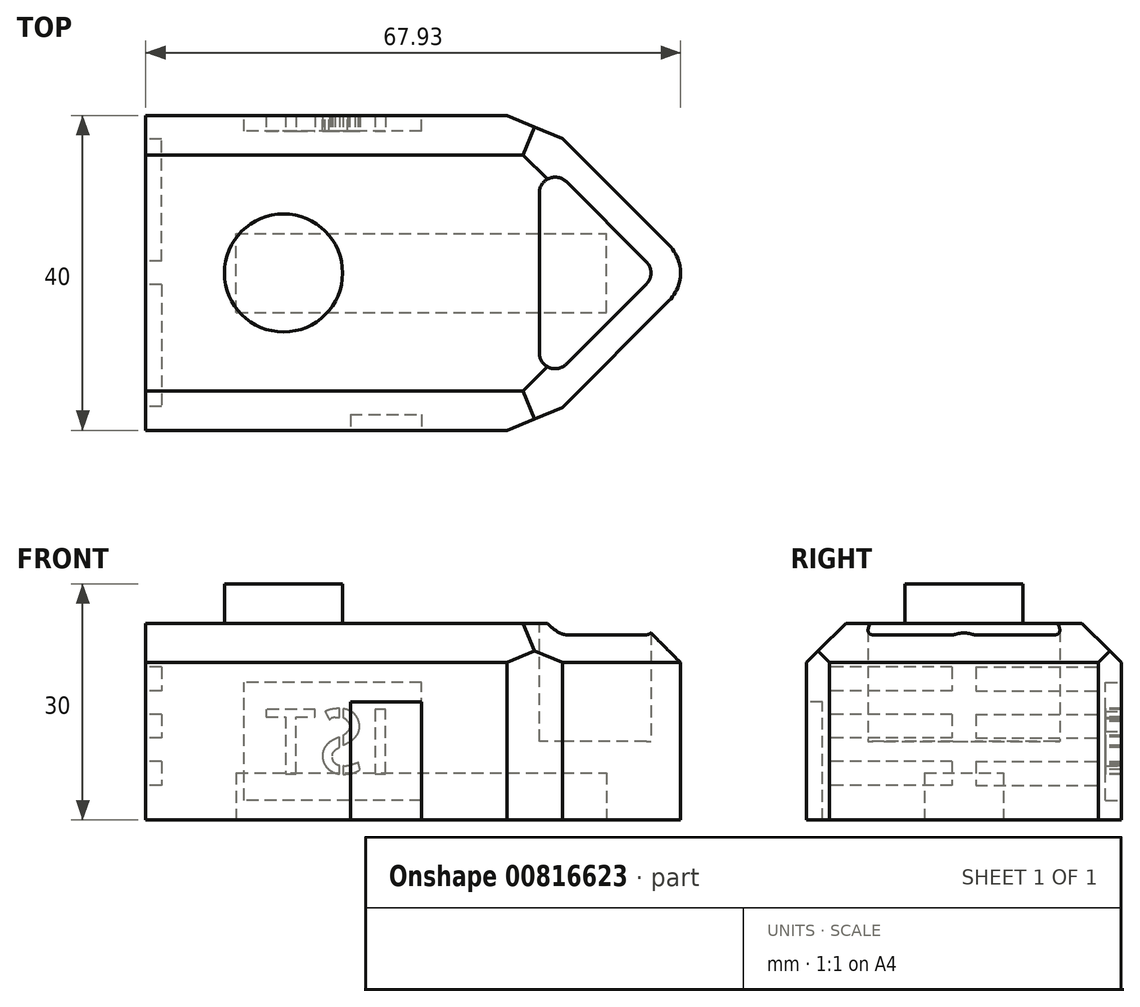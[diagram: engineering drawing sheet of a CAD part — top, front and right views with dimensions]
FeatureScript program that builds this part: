
annotation { "Feature Type Name" : "Feature", "Feature Type Description" : "" }
export const myFeature = defineFeature(function(context is Context, id is Id, definition is map)
    precondition{}
    {
        {
            var Q0;
            Q0=qCreatedBy(makeId("Top.planeOp"),FACE);
            var sketch = newSketch(context, id + "F0", { "sketchPlane" : qUnion([Q0])});
            skLineSegment(sketch, "E0.bottom", {"start": v(-35, 20) * mm, "end": v(35, 20) * mm});
            skLineSegment(sketch, "E0.top", {"start": v(-35, -20) * mm, "end": v(35, -20) * mm});
            skLineSegment(sketch, "E0.left", {"start": v(-35, 20) * mm, "end": v(-35, -20) * mm});
            skLineSegment(sketch, "E0.right", {"start": v(35, 20) * mm, "end": v(35, -20) * mm});
            skPoint(sketch, "E0.middle", {"position": v(0, 0) * mm});
            skSolve(sketch);
        }
        {
            var Q0;
            Q0 = qSketchRegion(id + "F0", true);
            extrude(context, id + "F1", {"entities" : qUnion([Q0]), "depth" : 25 * mm, "offsetDistance" : 25 * mm});
        }
        {
            var Q0;
            Q0=makeQuery(id+"F1.opExtrude","SWEPT_EDGE",EDGE,{"disambiguationData":[OSD([sQuery(id+"F0.wireOp",EDGE,"E0.top"),sQuery(id+"F0.wireOp",EDGE,"E0.right")])]});
            var Q1;
            Q1=makeQuery(id+"F1.opExtrude","SWEPT_EDGE",EDGE,{"disambiguationData":[OSD([sQuery(id+"F0.wireOp",EDGE,"E0.bottom"),sQuery(id+"F0.wireOp",EDGE,"E0.right")])]});
            chamfer(context, id + "F2", {"entities" : qUnion([Q0, Q1]), "width" : 20 * mm, "tangentPropagation" : true});
        }
        {
            var Q0;
            {var subQ0=sQuery(id+"F0.wireOp",EDGE,"E0.right");Q0=makeQuery(id+"F2.opChamfer","BLEND_EDGE",EDGE,{"blendedFrom":[makeQuery(id+"F1.opExtrude","SWEPT_EDGE",EDGE,{"disambiguationData":[OSD([sQuery(id+"F0.wireOp",EDGE,"E0.bottom"),subQ0])]}),makeQuery(id+"F1.opExtrude","SWEPT_EDGE",EDGE,{"disambiguationData":[OSD([sQuery(id+"F0.wireOp",EDGE,"E0.top"),subQ0])]})],"blendedInto":[]});}
            fillet(context, id + "F3", {"entities" : qUnion([Q0]), "radius" : 5 * mm, "tangentPropagation" : true, "allowEdgeOverflow" : false});
        }
        {
            var Q0;
            Q0=makeQuery(id+"F1.opExtrude","CAP_FACE",FACE,{"disambiguationData":[OSD([sQuery(id+"F0.wireOp",EDGE,"E0.bottom"),sQuery(id+"F0.wireOp",EDGE,"E0.top"),sQuery(id+"F0.wireOp",EDGE,"E0.left"),sQuery(id+"F0.wireOp",EDGE,"E0.right")])],"isStart":true});
            var sketch = newSketch(context, id + "F4", { "sketchPlane" : qUnion([Q0])});
            skLineSegment(sketch, "E1.bottom", {"start": v(-23.5, 5) * mm, "end": v(23.5, 5) * mm});
            skLineSegment(sketch, "E1.top", {"start": v(-23.5, -5) * mm, "end": v(23.5, -5) * mm});
            skLineSegment(sketch, "E1.left", {"start": v(-23.5, 5) * mm, "end": v(-23.5, -5) * mm});
            skLineSegment(sketch, "E1.right", {"start": v(23.5, 5) * mm, "end": v(23.5, -5) * mm});
            skPoint(sketch, "E1.middle", {"position": v(0, 0) * mm});
            skSolve(sketch);
        }
        {
            var Q0;
            Q0=makeQuery(id+"F4.imprint","IMPRINT",FACE,{"disambiguationData":[TD([[makeQuery(id+"F4.imprint","IMPRINT",EDGE,{"derivedFrom":sQuery(id+"F4.wireOp",EDGE,"E1.bottom")}),-1.0]])]});
            extrude(context, id + "F5", {"entities" : qUnion([Q0]), "operationType" : NewBodyOperationType.REMOVE, "oppositeDirection" : true, "depth" : 6 * mm, "offsetDistance" : 25 * mm});
        }
        {
            var Q0;
            Q0=makeQuery(id+"F1.opExtrude","CAP_FACE",FACE,{"disambiguationData":[OSD([sQuery(id+"F0.wireOp",EDGE,"E0.bottom"),sQuery(id+"F0.wireOp",EDGE,"E0.top"),sQuery(id+"F0.wireOp",EDGE,"E0.left"),sQuery(id+"F0.wireOp",EDGE,"E0.right")])],"isStart":false});
            var sketch = newSketch(context, id + "F6", { "sketchPlane" : qUnion([Q0])});
            skPoint(sketch, "E2", {"position": v(15, 0) * mm});
            skLineSegment(sketch, "E3", {"start": v(15, 0) * mm, "end": v(15, 15) * mm});
            skLineSegment(sketch, "E4", {"start": v(15, 15) * mm, "end": v(15, -15) * mm});
            skLineSegment(sketch, "E5", {"start": v(15, 15) * mm, "end": v(30, 0) * mm});
            skLineSegment(sketch, "E6", {"start": v(30, 0) * mm, "end": v(15, -15) * mm});
            skPoint(sketch, "E7.orphan", {"position": v(32.93, 0) * mm});
            skSolve(sketch);
        }
        {
            var Q0;
            Q0 = qSketchRegion(id + "F6", true);
            extrude(context, id + "F7", {"entities" : qUnion([Q0]), "operationType" : NewBodyOperationType.REMOVE, "oppositeDirection" : true, "depth" : 15 * mm, "offsetDistance" : 25 * mm});
        }
        {
            var Q0;
            Q0=makeQuery(id+"F7.boolean.opBoolean","COPY",EDGE,{"derivedFrom":makeQuery(id+"F7.opExtrude","CAP_EDGE",EDGE,{"disambiguationData":[OSD([sQuery(id+"F6.wireOp",EDGE,"E4")])],"isStart":true})});
            var Q1;
            Q1=makeQuery(id+"F7.boolean.opBoolean","COPY",EDGE,{"derivedFrom":makeQuery(id+"F7.opExtrude","SWEPT_EDGE",EDGE,{"disambiguationData":[OSD([sQuery(id+"F6.wireOp",EDGE,"E4"),sQuery(id+"F6.wireOp",EDGE,"E5")])]})});
            var Q2;
            Q2=makeQuery(id+"F7.boolean.opBoolean","COPY",EDGE,{"derivedFrom":makeQuery(id+"F7.opExtrude","SWEPT_EDGE",EDGE,{"disambiguationData":[OSD([sQuery(id+"F6.wireOp",EDGE,"E4"),sQuery(id+"F6.wireOp",EDGE,"E6")])]})});
            var Q3;
            Q3=makeQuery(id+"F7.boolean.opBoolean","COPY",EDGE,{"derivedFrom":makeQuery(id+"F7.opExtrude","SWEPT_EDGE",EDGE,{"disambiguationData":[OSD([sQuery(id+"F6.wireOp",EDGE,"E5"),sQuery(id+"F6.wireOp",EDGE,"E6")])]})});
            fillet(context, id + "F8", {"entities" : qUnion([Q0, Q1, Q2, Q3]), "radius" : 2 * mm, "tangentPropagation" : true, "allowEdgeOverflow" : false});
        }
        {
            var Q0;
            {var subQ0=sQuery(id+"F0.wireOp",EDGE,"E0.right");var subQ1=sQuery(id+"F0.wireOp",EDGE,"E0.bottom");Q0=makeQuery(id+"F2.opChamfer","BLEND_EDGE",EDGE,{"blendedFrom":[makeQuery(id+"F1.opExtrude","SWEPT_EDGE",EDGE,{"disambiguationData":[OSD([subQ1,subQ0])]}),makeQuery(id+"F1.opExtrude","CAP_FACE",FACE,{"disambiguationData":[OSD([subQ1,sQuery(id+"F0.wireOp",EDGE,"E0.top"),sQuery(id+"F0.wireOp",EDGE,"E0.left"),subQ0])],"isStart":false})],"blendedInto":[makeQuery(id+"F1.opExtrude","CAP_FACE",FACE,{"disambiguationData":[OSD([subQ1,sQuery(id+"F0.wireOp",EDGE,"E0.top"),sQuery(id+"F0.wireOp",EDGE,"E0.left"),subQ0])],"isStart":false})]});}
            chamfer(context, id + "F9", {"entities" : qUnion([Q0]), "width" : 5 * mm, "tangentPropagation" : true});
        }
        {
            var Q0;
            Q0=makeQuery(id+"F1.opExtrude","CAP_FACE",FACE,{"disambiguationData":[OSD([sQuery(id+"F0.wireOp",EDGE,"E0.bottom"),sQuery(id+"F0.wireOp",EDGE,"E0.top"),sQuery(id+"F0.wireOp",EDGE,"E0.left"),sQuery(id+"F0.wireOp",EDGE,"E0.right")])],"isStart":false});
            var sketch = newSketch(context, id + "F10", { "sketchPlane" : qUnion([Q0])});
            skCircle(sketch, "E8", {"center": v(-17.5, 0) * mm, "radius": 7.5 * mm});
            skPoint(sketch, "E9.orphan", {"position": v(0, 0) * mm});
            skPoint(sketch, "E10.orphan", {"position": v(-35, 0) * mm});
            skSolve(sketch);
        }
        {
            var Q0;
            Q0 = qSketchRegion(id + "F10", true);
            extrude(context, id + "F11", {"entities" : qUnion([Q0]), "operationType" : NewBodyOperationType.ADD, "depth" : 5 * mm, "offsetDistance" : 25 * mm});
        }
        {
            var Q0;
            Q0=makeQuery(id+"F1.opExtrude","SWEPT_FACE",FACE,{"disambiguationData":[OSD([sQuery(id+"F0.wireOp",EDGE,"E0.left")])]});
            var sketch = newSketch(context, id + "F12", { "sketchPlane" : qUnion([Q0])});
            skLineSegment(sketch, "E11", {"start": v(-1.5, 4.42) * mm, "end": v(-17, 4.42) * mm});
            skLineSegment(sketch, "E12", {"start": v(-17, 4.42) * mm, "end": v(-1.5, 4.42) * mm});
            skLineSegment(sketch, "E13", {"start": v(0, 7.42) * mm, "end": v(17, 7.42) * mm});
            skLineSegment(sketch, "E14", {"start": v(17, 7.42) * mm, "end": v(1.5, 7.42) * mm});
            skLineSegment(sketch, "E15", {"start": v(1.5, 10.42) * mm, "end": v(17, 10.42) * mm});
            skLineSegment(sketch, "E16", {"start": v(17, 10.42) * mm, "end": v(1.5, 10.42) * mm});
            skLineSegment(sketch, "E17", {"start": v(1.5, 13.42) * mm, "end": v(17, 13.42) * mm});
            skLineSegment(sketch, "E18", {"start": v(17, 13.42) * mm, "end": v(1.5, 13.42) * mm});
            skLineSegment(sketch, "E19", {"start": v(1.5, 16.42) * mm, "end": v(17, 16.42) * mm});
            skLineSegment(sketch, "E20", {"start": v(17, 16.42) * mm, "end": v(1.5, 16.42) * mm});
            skLineSegment(sketch, "E21", {"start": v(1.5, 19.42) * mm, "end": v(17, 19.42) * mm});
            skLineSegment(sketch, "E22", {"start": v(17, 19.42) * mm, "end": v(1.5, 19.42) * mm});
            skLineSegment(sketch, "E23", {"start": v(-17, 19.42) * mm, "end": v(-17, 16.42) * mm});
            skLineSegment(sketch, "E24", {"start": v(17, 19.42) * mm, "end": v(17, 16.42) * mm});
            skLineSegment(sketch, "E25", {"start": v(-1.5, 19.42) * mm, "end": v(-1.5, 16.42) * mm});
            skLineSegment(sketch, "E26", {"start": v(1.5, 19.42) * mm, "end": v(1.5, 16.42) * mm});
            skLineSegment(sketch, "E27.trimOffspring", {"start": v(-17, 13.42) * mm, "end": v(-17, 10.42) * mm});
            skLineSegment(sketch, "E28.trimOffspring", {"start": v(-17, 7.42) * mm, "end": v(-17, 4.42) * mm});
            skLineSegment(sketch, "E29.trimOffspring", {"start": v(-1.5, 13.42) * mm, "end": v(-1.5, 10.42) * mm});
            skLineSegment(sketch, "E30.trimOffspring", {"start": v(-1.5, 7.42) * mm, "end": v(-1.5, 4.42) * mm});
            skLineSegment(sketch, "E31.trimOffspring", {"start": v(1.5, 7.42) * mm, "end": v(1.5, 4.42) * mm});
            skLineSegment(sketch, "E32.trimOffspring", {"start": v(1.5, 13.42) * mm, "end": v(1.5, 10.42) * mm});
            skLineSegment(sketch, "E33.trimOffspring", {"start": v(-1.5, 19.42) * mm, "end": v(-17, 19.42) * mm});
            skLineSegment(sketch, "E34.trimOffspring", {"start": v(-1.5, 16.42) * mm, "end": v(-17, 16.42) * mm});
            skPoint(sketch, "E35.orphan", {"position": v(0, 19.42) * mm});
            skPoint(sketch, "E36.orphan", {"position": v(0, 16.42) * mm});
            skLineSegment(sketch, "E37.trimOffspring", {"start": v(-1.5, 13.42) * mm, "end": v(-17, 13.42) * mm});
            skLineSegment(sketch, "E38.trimOffspring", {"start": v(-1.5, 10.42) * mm, "end": v(-17, 10.42) * mm});
            skPoint(sketch, "E39.orphan", {"position": v(0, 13.42) * mm});
            skPoint(sketch, "E40.orphan", {"position": v(0, 10.42) * mm});
            skLineSegment(sketch, "E41.trimOffspring", {"start": v(-1.5, 7.42) * mm, "end": v(-17, 7.42) * mm});
            skLineSegment(sketch, "E42.trimOffspring", {"start": v(1.5, 4.42) * mm, "end": v(17, 4.42) * mm});
            skPoint(sketch, "E43.orphan", {"position": v(0, 4.42) * mm});
            skPoint(sketch, "E44.orphan", {"position": v(20, 19.42) * mm});
            skPoint(sketch, "E45.orphan", {"position": v(20, 16.42) * mm});
            skPoint(sketch, "E46.orphan", {"position": v(20, 13.42) * mm});
            skPoint(sketch, "E47.orphan", {"position": v(20, 10.42) * mm});
            skPoint(sketch, "E48.orphan", {"position": v(20, 4.42) * mm});
            skPoint(sketch, "E49.orphan", {"position": v(20, 7.42) * mm});
            skLineSegment(sketch, "E50.trimOffspring", {"start": v(17, 13.42) * mm, "end": v(17, 10.42) * mm});
            skLineSegment(sketch, "E51.trimOffspring", {"start": v(17, 7.42) * mm, "end": v(17, 4.42) * mm});
            skSolve(sketch);
        }
        {
            var Q0;
            Q0 = qSketchRegion(id + "F12", true);
            extrude(context, id + "F13", {"entities" : qUnion([Q0]), "operationType" : NewBodyOperationType.REMOVE, "oppositeDirection" : true, "depth" : 2 * mm, "offsetDistance" : 25 * mm});
        }
        {
            var Q0;
            Q0=makeQuery(id+"F1.opExtrude","CAP_EDGE",EDGE,{"disambiguationData":[OSD([sQuery(id+"F0.wireOp",EDGE,"E0.top")])],"isStart":false});
            var Q1;
            Q1=makeQuery(id+"F1.opExtrude","CAP_EDGE",EDGE,{"disambiguationData":[OSD([sQuery(id+"F0.wireOp",EDGE,"E0.bottom")])],"isStart":false});
            chamfer(context, id + "F14", {"entities" : qUnion([Q0, Q1]), "width" : 5 * mm, "tangentPropagation" : true});
        }
        {
            var Q0;
            Q0=makeQuery(id+"F1.opExtrude","SWEPT_FACE",FACE,{"disambiguationData":[OSD([sQuery(id+"F0.wireOp",EDGE,"E0.top")])]});
            var sketch = newSketch(context, id + "F15", { "sketchPlane" : qUnion([Q0])});
            skLineSegment(sketch, "E52.bottom", {"start": v(0, 0) * mm, "end": v(-9, 0) * mm});
            skLineSegment(sketch, "E52.top", {"start": v(0, 15) * mm, "end": v(-9, 15) * mm});
            skLineSegment(sketch, "E52.left", {"start": v(0, 0) * mm, "end": v(0, 15) * mm});
            skLineSegment(sketch, "E52.right", {"start": v(-9, 0) * mm, "end": v(-9, 15) * mm});
            skSolve(sketch);
        }
        {
            var Q0;
            Q0=makeQuery(id+"F15.imprint","IMPRINT",FACE,{"disambiguationData":[TD([[makeQuery(id+"F15.imprint","IMPRINT",EDGE,{"derivedFrom":sQuery(id+"F15.wireOp",EDGE,"E52.bottom")}),1.0]])]});
            extrude(context, id + "F16", {"entities" : qUnion([Q0]), "operationType" : NewBodyOperationType.REMOVE, "oppositeDirection" : true, "depth" : 2 * mm, "offsetDistance" : 25 * mm});
        }
        {
            var Q0;
            {var subQ0=sQuery(id+"F0.wireOp",EDGE,"E0.top");Q0=makeQuery(id+"F2.opChamfer","BLEND_EDGE",EDGE,{"blendedFrom":[makeQuery(id+"F1.opExtrude","SWEPT_EDGE",EDGE,{"disambiguationData":[OSD([subQ0,sQuery(id+"F0.wireOp",EDGE,"E0.right")])]}),makeQuery(id+"F1.opExtrude","SWEPT_FACE",FACE,{"disambiguationData":[OSD([subQ0])]})],"blendedInto":[makeQuery(id+"F1.opExtrude","SWEPT_FACE",FACE,{"disambiguationData":[OSD([subQ0])]})]});}
            var Q1;
            {var subQ0=sQuery(id+"F0.wireOp",EDGE,"E0.bottom");Q1=makeQuery(id+"F2.opChamfer","BLEND_EDGE",EDGE,{"blendedFrom":[makeQuery(id+"F1.opExtrude","SWEPT_EDGE",EDGE,{"disambiguationData":[OSD([subQ0,sQuery(id+"F0.wireOp",EDGE,"E0.right")])]}),makeQuery(id+"F1.opExtrude","SWEPT_FACE",FACE,{"disambiguationData":[OSD([subQ0])]})],"blendedInto":[makeQuery(id+"F1.opExtrude","SWEPT_FACE",FACE,{"disambiguationData":[OSD([subQ0])]})]});}
            chamfer(context, id + "F17", {"entities" : qUnion([Q0, Q1]), "width" : 10 * mm, "tangentPropagation" : true});
        }
        {
            var Q0;
            Q0=makeQuery(id+"F1.opExtrude","SWEPT_FACE",FACE,{"disambiguationData":[OSD([sQuery(id+"F0.wireOp",EDGE,"E0.bottom")])]});
            var sketch = newSketch(context, id + "F18", { "sketchPlane" : qUnion([Q0])});
            skLineSegment(sketch, "E53.bottom", {"start": v(0, 2.5) * mm, "end": v(22.5, 2.5) * mm});
            skLineSegment(sketch, "E53.top", {"start": v(0, 17.5) * mm, "end": v(22.5, 17.5) * mm});
            skLineSegment(sketch, "E53.left", {"start": v(0, 2.5) * mm, "end": v(0, 17.5) * mm});
            skLineSegment(sketch, "E53.right", {"start": v(22.5, 2.5) * mm, "end": v(22.5, 17.5) * mm});
            skSolve(sketch);
        }
        {
            var Q0;
            Q0 = qSketchRegion(id + "F18", true);
            extrude(context, id + "F19", {"entities" : qUnion([Q0]), "operationType" : NewBodyOperationType.REMOVE, "oppositeDirection" : true, "depth" : 2 * mm, "offsetDistance" : 25 * mm});
        }
        {
            var Q0;
            Q0=makeQuery(id+"F19.boolean.opBoolean","COPY",FACE,{"derivedFrom":makeQuery(id+"F19.opExtrude","CAP_FACE",FACE,{"disambiguationData":[OSD([sQuery(id+"F18.wireOp",EDGE,"E53.bottom"),sQuery(id+"F18.wireOp",EDGE,"E53.top"),sQuery(id+"F18.wireOp",EDGE,"E53.left"),sQuery(id+"F18.wireOp",EDGE,"E53.right")])],"isStart":false})});
            var sketch = newSketch(context, id + "F20", { "sketchPlane" : qUnion([Q0])});
            skText(sketch, "E54", { "text": "IST\n", "fontName": "AllertaStencil-Regular.ttf"});
            const initialGuessF20  = {"E54": [0.00348, 0.00586, 1, 0, 0.00818]};
            skSetInitialGuess(sketch, initialGuessF20);
            skSolve(sketch);
        }
        {
            var Q0;
            Q0 = qSketchRegion(id + "F20", true);
            extrude(context, id + "F21", {"entities" : qUnion([Q0]), "operationType" : NewBodyOperationType.ADD, "depth" : 2 * mm, "offsetDistance" : 25 * mm});
        }
    });
